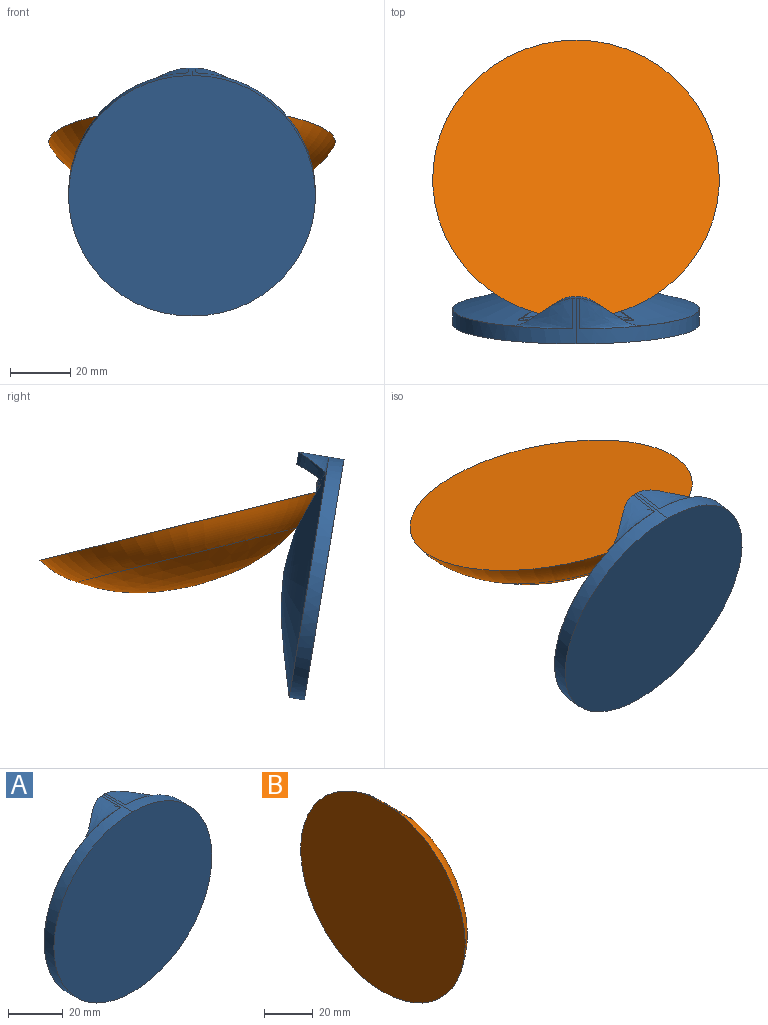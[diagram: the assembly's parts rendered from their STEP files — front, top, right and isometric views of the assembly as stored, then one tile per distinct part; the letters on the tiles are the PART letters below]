
ASSEMBLY  parts=2 mates=1
PART A: 27 faces, bbox 82.2x15.5x81.1 mm
  f0: revolved ~80.67x80.67mm, area 2384.7mm2, adj f1,f3,f4,f5,f6,f7,f8,f18
  f1: revolved ~80.67x80.67mm, area 2382.6mm2, adj f0,f3,f12,f13,f14,f15,f16,f18
  f2: cylinder r=40.4mm len=80.79mm, axis (0,1,0), area 661.6mm2, adj f3,f5,f9,f10,f11
  f3: plane 81.96x74.73mm, normal (0,1,0), area 12.8mm2, adj f0,f1,f2,f6,f11,f14
  f4: cylinder r=36.3mm len=9.03mm, axis (0,-1,0), area 10mm2, adj f0,f8,f10,f12
  f5: bspline ~20.86x10.16mm, area 114.1mm2, adj f0,f2,f6,f7
  f6: bspline ~0.37x0.15mm, area 0mm2, adj f0,f3,f5
  f7: bspline ~20.86x10.16mm, area 82.6mm2, adj f0,f5,f8,f10
  f8: bspline ~18.44x10.16mm, area 52.5mm2, adj f0,f4,f7
  f9: plane 81.9x80.79mm, normal (0,-1,0), area 5216mm2, adj f2,f11
  f10: plane 4.1x2.22mm, normal (0,1,0), area 9.1mm2, adj f2,f4,f7,f11,f12,f15
  f11: cylinder r=40.4mm len=80.79mm, axis (0,1,0), area 661.6mm2, adj f2,f3,f9,f10,f13
  f12: cylinder r=36.3mm len=9.03mm, axis (0,-1,0), area 10mm2, adj f1,f4,f10,f16
  f13: bspline ~20.86x10.16mm, area 114.1mm2, adj f1,f11,f14,f15
  f14: bspline ~0.37x0.15mm, area 0mm2, adj f1,f3,f13
  f15: bspline ~20.86x10.16mm, area 82.6mm2, adj f1,f10,f13,f16
  f16: bspline ~18.44x10.16mm, area 52.5mm2, adj f1,f12,f15
  f17: plane 36.44x13.1mm, normal (0,0.94,0.34), area 277.7mm2, adj f18,f21,f22,f23,f25
  f18: plane 8.95x0.38mm, normal (0,-0.05,1), area 0.4mm2, adj f0,f1,f17,f23,f25
  f19: bspline ~26.89x5.3mm, area 18.9mm2, adj f1,f20,f22
  f20: bspline ~24.61x5.33mm, area 18.9mm2, adj f0,f19,f21
  f21: bspline ~20.83x4.26mm, area 47.4mm2, adj f17,f20,f22,f26
  f22: bspline ~22.05x4.36mm, area 47.4mm2, adj f17,f19,f21,f24
  f23: bspline ~19.85x16.44mm, area 4.3mm2, adj f1,f17,f18,f24
  f24: bspline ~2.47x1.53mm, area 0.2mm2, adj f1,f22,f23
  f25: bspline ~19.85x16.44mm, area 4.3mm2, adj f0,f17,f18,f26
  f26: bspline ~2.6x1.67mm, area 0.2mm2, adj f0,f21,f25
PART B: 4 faces, bbox 20.5x95.1x95.1 mm
  f0: revolved ~95.07x95.07mm, area 3574.3mm2, adj f1,f2,f3
  f1: plane 95.07x94.52mm, normal (-1,0,0), area 7093mm2, adj f0,f3
  f2: revolved ~75.16x75.16mm, area 4810.7mm2, adj f0
  f3: plane 22.35x9.96mm, normal (0.69,0,0.73), area 252.6mm2, adj f0,f1
PLACE A rot(axis=(1,0,0),9.4deg) t=(-5.12,17.82,20.88)mm
PLACE B rot(axis=(0.52,0.52,-0.67),112.4deg) t=(-5.68,60.91,37.91)mm
MATE planar B.f3 <-> A.f17  axis (0,-0.87,-0.49) through (-5.68,18.46,43.54)mm
